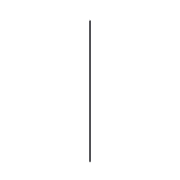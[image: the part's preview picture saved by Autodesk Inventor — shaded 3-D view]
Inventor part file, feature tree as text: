
AUTODESK INVENTOR PART (.ipt)
format: ipt  version: 2016 (Build 200138000, 138)  size: 71,680 bytes
history: native  units: in
note: dims shown in document units (in); Inventor stores cm internally (conversion verified against a paired STEP export)
features: other x1, extrude x1, chamfer x1, sketch x1
ambient origin geometry x8: Origin, YZ Plane, XZ Plane, XY Plane, X Axis, Y Axis, Z Axis, Center Point
bodies: Solid1 (feature_tree)
feature tree (4):
  other  "skeleton.ipt"
  extrude  "Extrusion1"  Depth=0.3937in
  chamfer  "Chamfer1"  Distance=11.811in
  sketch  "Sketch1"  dims[d0=0.1181in d1=0.3937in d2=11.811in d3=0.0in d5=0.0197in d6=0.0787in d7=45.0deg]
